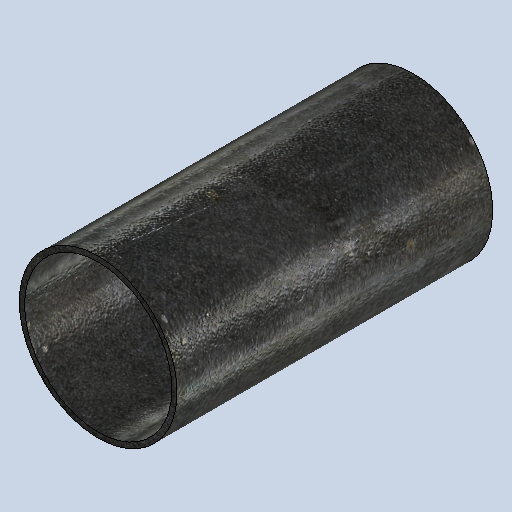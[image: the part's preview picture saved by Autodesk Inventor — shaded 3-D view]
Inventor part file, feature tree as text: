
AUTODESK INVENTOR PART (.ipt)
format: ipt  version: 2025 (Build 290162010, 162A)  size: 307,200 bytes
history: native  units: mm
features: extrude x1, sketch x1
ambient origin geometry x8: Origin, YZ Plane, XZ Plane, XY Plane, X Axis, Y Axis, Z Axis, Center Point
bodies: Solid1 (feature_tree)
feature tree (2):
  extrude  "Extrusion1"  Depth=180.0mm
  sketch  "Sketch1"  dims[d0=90.0mm d1=3.0mm d2=180.0mm d3=0.0mm]
